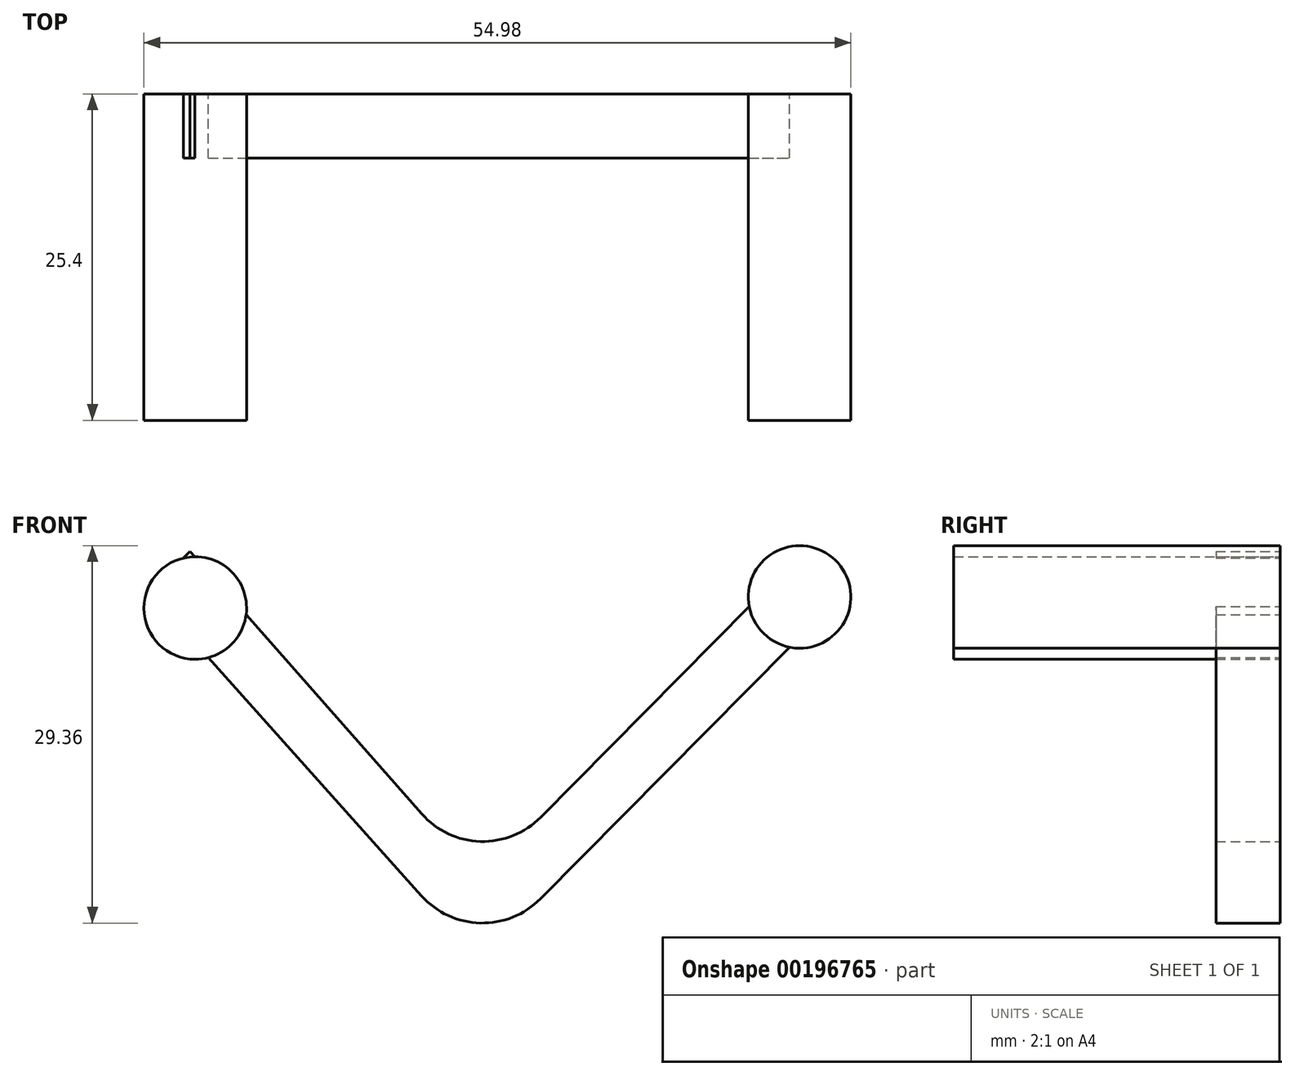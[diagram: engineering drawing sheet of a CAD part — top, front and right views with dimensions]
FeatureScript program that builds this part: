
annotation { "Feature Type Name" : "Feature", "Feature Type Description" : "" }
export const myFeature = defineFeature(function(context is Context, id is Id, definition is map)
    precondition{}
    {
        {
            var Q0;
            Q0=qCreatedBy(makeId("Front.planeOp"),FACE);
            var sketch = newSketch(context, id + "F0", { "sketchPlane" : qUnion([Q0])});
            skLineSegment(sketch, "E0", {"start": v(-22.5, 42.4) * mm, "end": v(-4.5, 21.98) * mm});
            skLineSegment(sketch, "E1", {"start": v(4.78, 21.71) * mm, "end": v(25.25, 42.4) * mm});
            skLineSegment(sketch, "E2", {"start": v(-22.5, 42.4) * mm, "end": v(-25.65, 39.23) * mm});
            skLineSegment(sketch, "E3", {"start": v(-25.65, 39.23) * mm, "end": v(-4.5, 15.6) * mm});
            skLineSegment(sketch, "E4", {"start": v(4.75, 15.36) * mm, "end": v(28.35, 39.23) * mm});
            skLineSegment(sketch, "E5", {"start": v(25.25, 42.4) * mm, "end": v(28.35, 39.23) * mm});
            skPoint(sketch, "E6.visualSharp", {"position": v(0, 10.57) * mm});
            skArc(sketch, "E6.filletArc", {"start": v(-4.5, 15.6) * mm, "mid": v(0.07, 13.48) * mm, "end": v(4.75, 15.36) * mm});
            skPoint(sketch, "E7.visualSharp", {"position": v(0, 16.88) * mm});
            skArc(sketch, "E7.filletArc", {"start": v(-4.5, 21.98) * mm, "mid": v(0.08, 19.83) * mm, "end": v(4.78, 21.71) * mm});
            skSolve(sketch);
        }
        {
            var Q0;
            Q0=makeQuery(id+"F0.imprint","IMPRINT",FACE,{"disambiguationData":[TD([[makeQuery(id+"F0.imprint","IMPRINT",EDGE,{"derivedFrom":sQuery(id+"F0.wireOp",EDGE,"E0")}),-1.0]])]});
            var sketch = newSketch(context, id + "F1", { "sketchPlane" : qUnion([Q0])});
            skCircle(sketch, "E8", {"center": v(-22.1, 38) * mm, "radius": 4 * mm});
            skCircle(sketch, "E9", {"center": v(24.9, 38.85) * mm, "radius": 3.99 * mm});
            skSolve(sketch);
        }
        {
            var Q0;
            Q0 = qSketchRegion(id + "F0", true);
            extrude(context, id + "F2", {"entities" : qUnion([Q0]), "depth" : 5 * mm});
        }
        {
            var Q0;
            Q0 = qSketchRegion(id + "F1", true);
            extrude(context, id + "F3", {"entities" : qUnion([Q0]), "operationType" : NewBodyOperationType.ADD, "depth" : 25.4 * mm});
        }
    });
